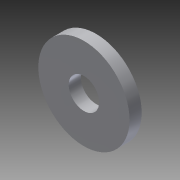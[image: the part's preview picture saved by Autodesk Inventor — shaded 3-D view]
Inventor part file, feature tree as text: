
AUTODESK INVENTOR PART (.ipt)
format: ipt  version: 2014 SP1 (Build 180222100, 222)  size: 78,336 bytes
history: native  units: in
note: dims shown in document units (in); Inventor stores cm internally (conversion verified against a paired STEP export)
features: extrude x1, sketch x1
ambient origin geometry x8: Origin, YZ Plane, XZ Plane, XY Plane, X Axis, Y Axis, Z Axis, Center Point
bodies: Solid1 (feature_tree)
feature tree (2):
  extrude  "Extrusion1"  Depth=0.0787in
  sketch  "Sketch1"  dims[d0=0.1969in d1=0.5906in d2=0.0787in d3=0.0in]
